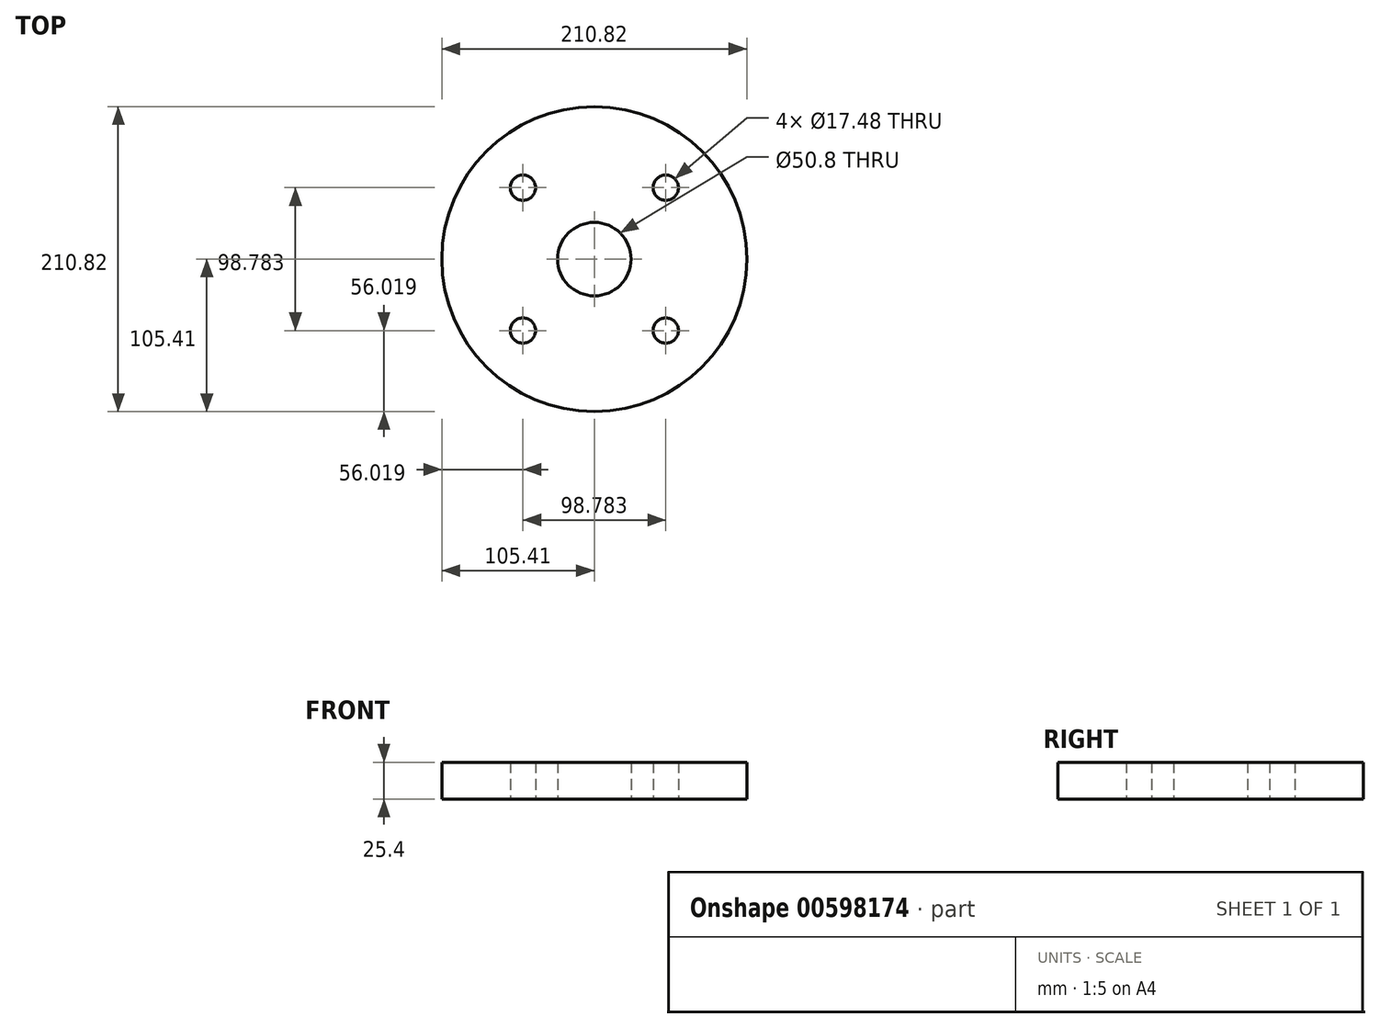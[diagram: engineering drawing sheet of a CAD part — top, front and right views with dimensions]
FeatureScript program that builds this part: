
annotation { "Feature Type Name" : "Feature", "Feature Type Description" : "" }
export const myFeature = defineFeature(function(context is Context, id is Id, definition is map)
    precondition{}
    {
        {
            var Q0;
            Q0=qCreatedBy(makeId("Top.planeOp"),FACE);
            var sketch = newSketch(context, id + "F0", { "sketchPlane" : qUnion([Q0])});
            skLineSegment(sketch, "E0", {"start": v(0, 0) * mm, "end": v(95.46, 0) * mm, "construction": true});
            skLineSegment(sketch, "E1.1.1", {"start": v(0.21, 0.4) * mm, "end": v(0.39, 89.2) * mm, "construction": true});
            skLineSegment(sketch, "E1.2.1", {"start": v(0, 0) * mm, "end": v(-89.16, 0.01) * mm, "construction": true});
            skPoint(sketch, "E1.center", {"position": v(0, 0) * mm});
            skLineSegment(sketch, "E2.2.3.0", {"start": v(0, 0) * mm, "end": v(0, -89.16) * mm, "construction": true});
            skCircle(sketch, "E3", {"center": v(0, 0) * mm, "radius": 69.85 * mm, "construction": true});
            skLineSegment(sketch, "E4", {"start": v(0, 0) * mm, "end": v(63.75, 63.75) * mm, "construction": true});
            skCircle(sketch, "E5", {"center": v(49.4, 49.4) * mm, "radius": 8.74 * mm});
            skCircle(sketch, "E6.1.0", {"center": v(-49.4, 49.4) * mm, "radius": 8.74 * mm});
            skLineSegment(sketch, "E6.1.1", {"start": v(0, 0) * mm, "end": v(-63.75, 63.75) * mm, "construction": true});
            skCircle(sketch, "E6.2.0", {"center": v(-49.4, -49.4) * mm, "radius": 8.74 * mm});
            skLineSegment(sketch, "E6.2.1", {"start": v(0, 0) * mm, "end": v(-63.75, -63.75) * mm, "construction": true});
            skCircle(sketch, "E7.1.3.0", {"center": v(49.4, -49.4) * mm, "radius": 8.74 * mm});
            skLineSegment(sketch, "E7.2.3.0", {"start": v(0, 0) * mm, "end": v(63.75, -63.75) * mm, "construction": true});
            skCircle(sketch, "E8", {"center": v(0, 0) * mm, "radius": 25.4 * mm});
            skLineSegment(sketch, "E9.0", {"start": v(95.46, 0) * mm, "end": v(95.64, 89.2) * mm, "construction": true});
            skLineSegment(sketch, "E10.0", {"start": v(-95.04, 0.41) * mm, "end": v(-94.83, 104.92) * mm, "construction": true});
            skLineSegment(sketch, "E11.0", {"start": v(0, 95.25) * mm, "end": v(-111.04, 95.27) * mm, "construction": true});
            skCircle(sketch, "E12", {"center": v(-94.85, 95.27) * mm, "radius": 20.96 * mm, "construction": true});
            skCircle(sketch, "E13", {"center": v(0, 0) * mm, "radius": 105.41 * mm});
            skSolve(sketch);
        }
        {
            var Q0;
            Q0 = qSketchRegion(id + "F0", true);
            extrude(context, id + "F1", {"entities" : qUnion([Q0]), "depth" : 25.4 * mm, "offsetDistance" : 25.4 * mm});
        }
    });
